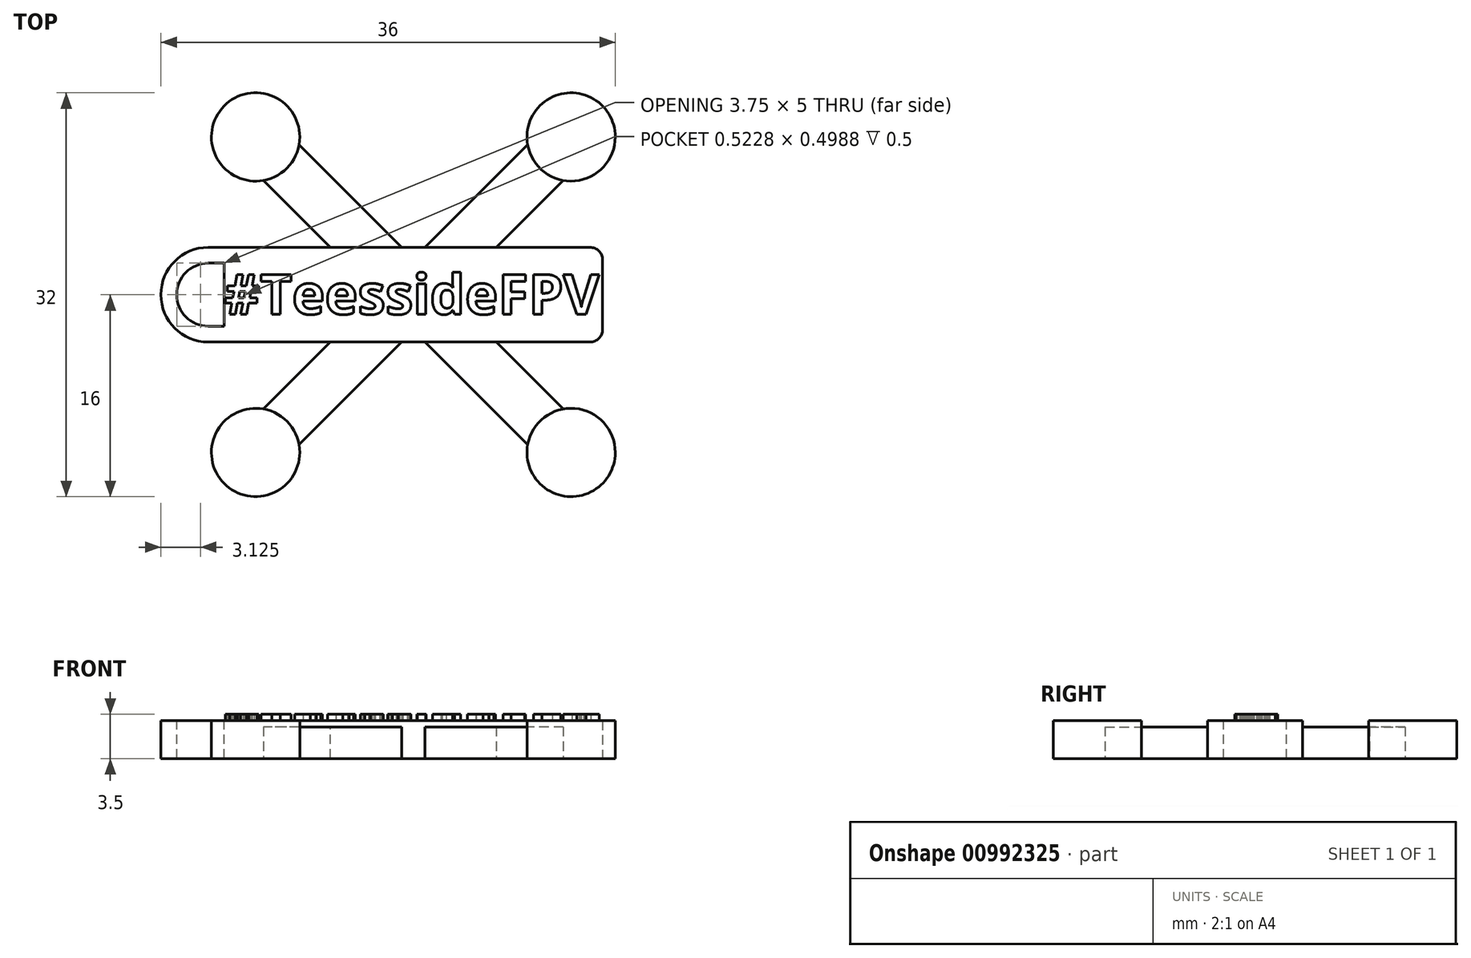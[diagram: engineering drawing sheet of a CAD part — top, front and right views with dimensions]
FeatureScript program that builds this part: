
annotation { "Feature Type Name" : "Feature", "Feature Type Description" : "" }
export const myFeature = defineFeature(function(context is Context, id is Id, definition is map)
    precondition{}
    {
        {
            assignVariable(context, id + "F0", {"name" : "Length", "anyValue" : 30});
        }
        {
            var Q0;
            Q0=qCreatedBy(makeId("Top.planeOp"),FACE);
            var sketch = newSketch(context, id + "F1", { "sketchPlane" : qUnion([Q0])});
            skLineSegment(sketch, "E0.bottom", {"start": v(15, -3.75) * mm, "end": v(-15, -3.75) * mm});
            skLineSegment(sketch, "E0.top", {"start": v(15, 3.75) * mm, "end": v(-15, 3.75) * mm});
            skLineSegment(sketch, "E0.left", {"start": v(15, -3.75) * mm, "end": v(15, 3.75) * mm});
            skLineSegment(sketch, "E0.right", {"start": v(-15, -3.75) * mm, "end": v(-15, 3.75) * mm});
            skPoint(sketch, "E0.middle", {"position": v(0, 0) * mm});
            skCircle(sketch, "E1", {"center": v(-12.5, 12.5) * mm, "radius": 3.5 * mm});
            skCircle(sketch, "E2", {"center": v(-12.5, -12.5) * mm, "radius": 3.5 * mm});
            skCircle(sketch, "E3", {"center": v(12.5, -12.5) * mm, "radius": 3.5 * mm});
            skCircle(sketch, "E4", {"center": v(12.5, 12.5) * mm, "radius": 3.5 * mm});
            skSolve(sketch);
        }
        {
            var Q0;
            Q0=qSketchRegion(id+"F1",true);
            extrude(context, id + "F2", {"entities" : qUnion([Q0]), "depth" : 3 * mm, "offsetDistance" : 25 * mm});
        }
        {
            var Q0;
            Q0=makeQuery(id+"F2.opExtrude","CAP_FACE",FACE,{"disambiguationData":[OSD([sQuery(id+"F1.wireOp",EDGE,"E0.bottom"),sQuery(id+"F1.wireOp",EDGE,"E0.top"),sQuery(id+"F1.wireOp",EDGE,"E0.left"),sQuery(id+"F1.wireOp",EDGE,"E0.right")])],"isStart":false});
            var sketch = newSketch(context, id + "F3", { "sketchPlane" : qUnion([Q0])});
            skText(sketch, "E5", { "text": "#TeessideFPV", "fontName": "OpenSans-Bold.ttf"});
            const initialGuessF3  = {"E5": [-0.015, -0.00155, 1, 0, 0.00317]};
            skSetInitialGuess(sketch, initialGuessF3);
            skSolve(sketch);
        }
        {
            var Q0;
            Q0=qSketchRegion(id+"F3",true);
            extrude(context, id + "F4", {"entities" : qUnion([Q0]), "operationType" : NewBodyOperationType.ADD, "depth" : 0.5 * mm, "offsetDistance" : 25 * mm});
        }
        {
            var Q0;
            Q0=makeQuery(id+"F2.opExtrude","CAP_FACE",FACE,{"disambiguationData":[OSD([sQuery(id+"F1.wireOp",EDGE,"E0.bottom"),sQuery(id+"F1.wireOp",EDGE,"E0.top"),sQuery(id+"F1.wireOp",EDGE,"E0.left"),sQuery(id+"F1.wireOp",EDGE,"E0.right")])],"isStart":true});
            var sketch = newSketch(context, id + "F5", { "sketchPlane" : qUnion([Q0])});
            skLineSegment(sketch, "E6.bottom", {"start": v(11.09, 13.91) * mm, "end": v(-13.91, -11.09) * mm});
            skLineSegment(sketch, "E6.top", {"start": v(13.91, 11.09) * mm, "end": v(-11.09, -13.91) * mm});
            skLineSegment(sketch, "E6.left", {"start": v(11.09, 13.91) * mm, "end": v(13.91, 11.09) * mm});
            skLineSegment(sketch, "E6.right", {"start": v(-13.91, -11.09) * mm, "end": v(-11.09, -13.91) * mm});
            skPoint(sketch, "E6.middle", {"position": v(0, 0) * mm});
            skLineSegment(sketch, "E7.bottom", {"start": v(13.91, -11.09) * mm, "end": v(-11.09, 13.91) * mm});
            skLineSegment(sketch, "E7.top", {"start": v(11.09, -13.91) * mm, "end": v(-13.91, 11.09) * mm});
            skLineSegment(sketch, "E7.left", {"start": v(13.91, -11.09) * mm, "end": v(11.09, -13.91) * mm});
            skLineSegment(sketch, "E7.right", {"start": v(-11.09, 13.91) * mm, "end": v(-13.91, 11.09) * mm});
            skSolve(sketch);
        }
        {
            var Q0;
            Q0=qSketchRegion(id+"F5",true);
            extrude(context, id + "F6", {"entities" : qUnion([Q0]), "operationType" : NewBodyOperationType.ADD, "oppositeDirection" : true, "depth" : 2.5 * mm, "offsetDistance" : 25 * mm});
        }
        {
            var Q0;
            Q0=makeQuery(id+"F2.opExtrude","SWEPT_FACE",FACE,{"disambiguationData":[OSD([sQuery(id+"F1.wireOp",EDGE,"E0.right")])]});
            extrude(context, id + "F7", {"entities" : qUnion([Q0]), "operationType" : NewBodyOperationType.ADD, "depth" : 5 * mm, "offsetDistance" : 25 * mm});
        }
        {
            var Q0;
            Q0=makeQuery(id+"F7.opExtrude","CAP_EDGE",EDGE,{"disambiguationData":[OSD([sQuery(id+"F1.wireOp",EDGE,"E0.top"),sQuery(id+"F1.wireOp",EDGE,"E0.right")])],"isStart":false});
            var Q1;
            Q1=makeQuery(id+"F7.opExtrude","CAP_EDGE",EDGE,{"disambiguationData":[OSD([sQuery(id+"F1.wireOp",EDGE,"E0.bottom"),sQuery(id+"F1.wireOp",EDGE,"E0.right")])],"isStart":false});
            fillet(context, id + "F8", {"entities" : qUnion([Q0, Q1]), "radius" : (getVariable(context, 'Length') / 8) * mm, "tangentPropagation" : true, "allowEdgeOverflow" : false});
        }
        {
            var Q0;
            {var subQ0=sQuery(id+"F1.wireOp",EDGE,"E0.right");var subQ1=sQuery(id+"F1.wireOp",EDGE,"E0.top");var subQ2=sQuery(id+"F1.wireOp",EDGE,"E0.bottom");var subQ3=sQuery(id+"F1.wireOp",EDGE,"E0.left");Q0=makeQuery(id+"F7.boolean.opBoolean","MERGE",FACE,{"derivedFrom":[makeQuery(id+"F4.boolean.opBoolean","SPLIT",FACE,{"disambiguationData":[TD([makeQuery(id+"F2.opExtrude","SWEPT_FACE",FACE,{"disambiguationData":[OSD([subQ2])]})])],"derivedFrom":makeQuery(id+"F2.opExtrude","CAP_FACE",FACE,{"disambiguationData":[OSD([subQ2,subQ1,subQ3,subQ0])],"isStart":false})}),makeQuery(id+"F7.opExtrude","SWEPT_FACE",FACE,{"disambiguationData":[OSD([subQ0]),TDD([makeQuery(id+"F2.opExtrude","CAP_EDGE",EDGE,{"disambiguationData":[OSD([subQ0])],"isStart":false})])]})]});}
            var sketch = newSketch(context, id + "F9", { "sketchPlane" : qUnion([Q0])});
            skArc(sketch, "E8", {"start": v(-16.25, 2.5) * mm, "mid": v(-18.75, 0) * mm, "end": v(-16.25, -2.5) * mm});
            skLineSegment(sketch, "E9", {"start": v(-16.25, 2.5) * mm, "end": v(-15, 2.5) * mm});
            skLineSegment(sketch, "E10", {"start": v(-16.25, -2.5) * mm, "end": v(-15, -2.5) * mm});
            skLineSegment(sketch, "E11.3", {"start": v(-15, -2.5) * mm, "end": v(-15, 2.5) * mm});
            skPoint(sketch, "E11.4", {"position": v(0, 0) * mm});
            skPoint(sketch, "E11.1.end.orphan", {"position": v(-15, 3.75) * mm});
            skPoint(sketch, "E11.1.start.orphan", {"position": v(15, 3.75) * mm});
            skPoint(sketch, "E11.2.end.orphan", {"position": v(15, 3.75) * mm});
            skPoint(sketch, "E11.2.start.orphan", {"position": v(15, -3.75) * mm});
            skPoint(sketch, "E11.0.end.orphan", {"position": v(-15, -3.75) * mm});
            skPoint(sketch, "E11.0.start.orphan", {"position": v(15, -3.75) * mm});
            skSolve(sketch);
        }
        {
            var Q0;
            Q0=qSketchRegion(id+"F9",true);
            extrude(context, id + "F10", {"entities" : qUnion([Q0]), "operationType" : NewBodyOperationType.REMOVE, "oppositeDirection" : true, "depth" : 25 * mm, "offsetDistance" : 25 * mm});
        }
        {
            var Q0;
            Q0=makeQuery(id+"F2.opExtrude","SWEPT_EDGE",EDGE,{"disambiguationData":[OSD([sQuery(id+"F1.wireOp",EDGE,"E0.bottom"),sQuery(id+"F1.wireOp",EDGE,"E0.left")])]});
            var Q1;
            Q1=makeQuery(id+"F2.opExtrude","SWEPT_EDGE",EDGE,{"disambiguationData":[OSD([sQuery(id+"F1.wireOp",EDGE,"E0.top"),sQuery(id+"F1.wireOp",EDGE,"E0.left")])]});
            fillet(context, id + "F11", {"entities" : qUnion([Q0, Q1]), "radius" : 1 * mm, "tangentPropagation" : true, "allowEdgeOverflow" : false});
        }
    });
